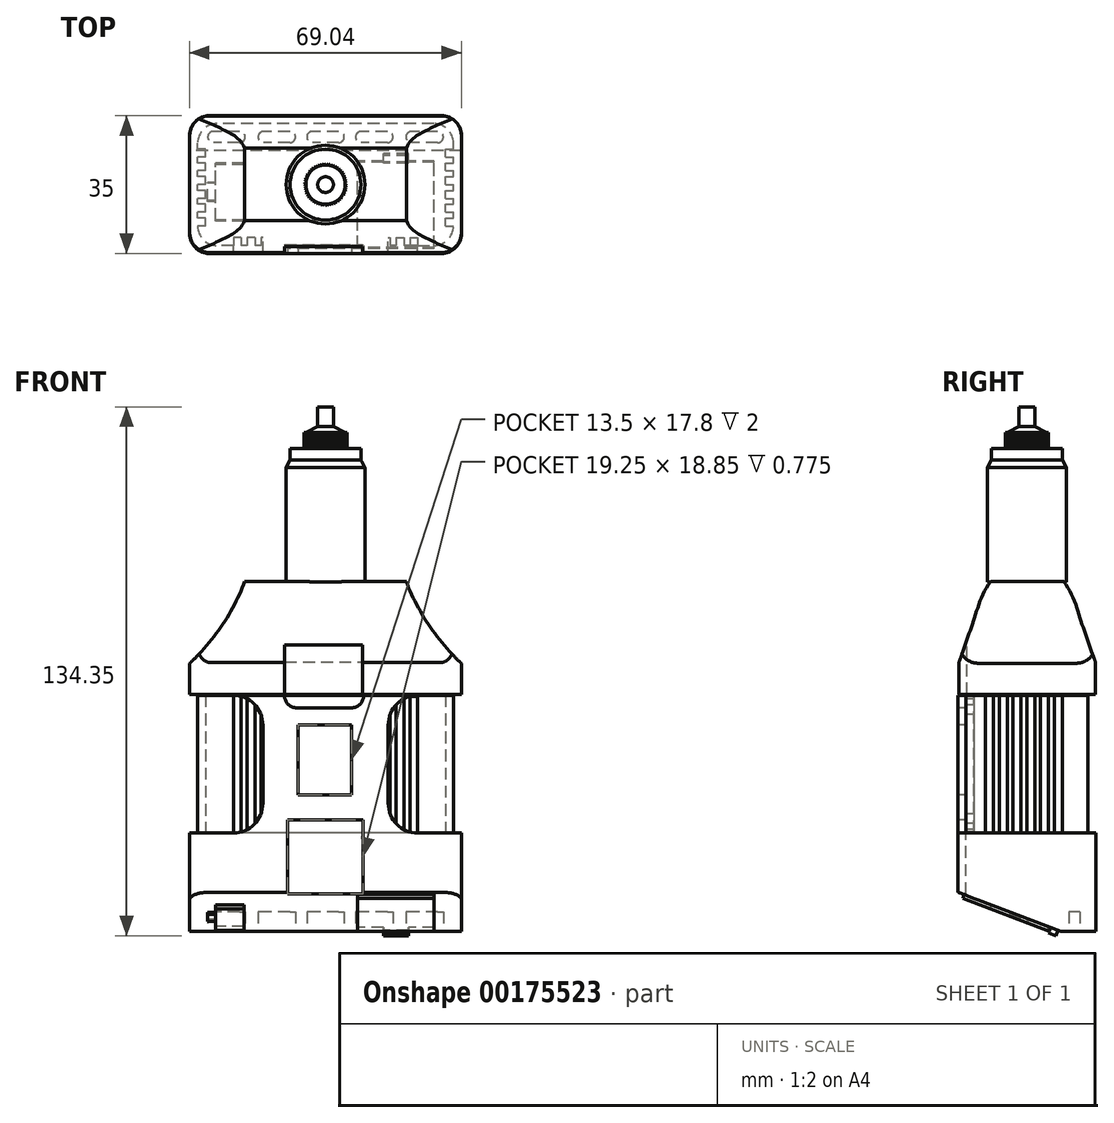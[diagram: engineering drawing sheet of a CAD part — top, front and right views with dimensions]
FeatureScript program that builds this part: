
annotation { "Feature Type Name" : "Feature", "Feature Type Description" : "" }
export const myFeature = defineFeature(function(context is Context, id is Id, definition is map)
    precondition{}
    {
        {
            var Q0;
            Q0=qCreatedBy(makeId("Front.planeOp"),FACE);
            var sketch = newSketch(context, id + "F0", { "sketchPlane" : qUnion([Q0])});
            skLineSegment(sketch, "E0.bottom", {"start": v(32.52, 25.25) * mm, "end": v(-32.53, 25.25) * mm});
            skLineSegment(sketch, "E0.top", {"start": v(32.53, -25.25) * mm, "end": v(-32.52, -25.25) * mm});
            skLineSegment(sketch, "E0.left", {"start": v(32.52, 25.25) * mm, "end": v(32.53, -25.25) * mm});
            skLineSegment(sketch, "E0.right", {"start": v(-32.53, 25.25) * mm, "end": v(-32.52, -25.25) * mm});
            skPoint(sketch, "E0.middle", {"position": v(0, 0) * mm});
            skSolve(sketch);
        }
        {
            var Q0;
            Q0=makeQuery(id+"F0.imprint","IMPRINT",FACE,{"disambiguationData":[TD([[makeQuery(id+"F0.imprint","IMPRINT",EDGE,{"derivedFrom":sQuery(id+"F0.wireOp",EDGE,"E0.bottom")}),1.0]])]});
            extrude(context, id + "F1", {"entities" : qUnion([Q0]), "endBound" : BoundingType.SYMMETRIC, "depth" : 31 * mm});
        }
        {
            var Q0;
            Q0=makeQuery(id+"F1.opExtrude","CAP_FACE",FACE,{"disambiguationData":[OSD([sQuery(id+"F0.wireOp",EDGE,"E0.bottom"),sQuery(id+"F0.wireOp",EDGE,"E0.top"),sQuery(id+"F0.wireOp",EDGE,"E0.left"),sQuery(id+"F0.wireOp",EDGE,"E0.right")])],"isStart":false});
            var sketch = newSketch(context, id + "F2", { "sketchPlane" : qUnion([Q0])});
            skLineSegment(sketch, "E1", {"start": v(-32.52, -9.75) * mm, "end": v(-23.43, -9.75) * mm});
            skLineSegment(sketch, "E2", {"start": v(-32.52, -25.25) * mm, "end": v(32.53, -25.25) * mm});
            skLineSegment(sketch, "E3", {"start": v(-15.93, 17.75) * mm, "end": v(-15.92, -2.25) * mm});
            skLineSegment(sketch, "E4", {"start": v(15.92, 17.75) * mm, "end": v(15.92, -2.25) * mm});
            skLineSegment(sketch, "E5", {"start": v(-32.52, -9.75) * mm, "end": v(-32.52, -25.25) * mm});
            skLineSegment(sketch, "E6", {"start": v(32.53, -9.75) * mm, "end": v(32.53, -25.25) * mm});
            skLineSegment(sketch, "E7.trimOffspring", {"start": v(23.43, -9.75) * mm, "end": v(32.53, -9.75) * mm});
            skArc(sketch, "E8", {"start": v(-23.43, -9.75) * mm, "mid": v(-18.12, -7.55) * mm, "end": v(-15.92, -2.25) * mm});
            skArc(sketch, "E9", {"start": v(15.92, -2.25) * mm, "mid": v(18.12, -7.55) * mm, "end": v(23.43, -9.75) * mm});
            skPoint(sketch, "E10.orphan", {"position": v(-15.93, 25.25) * mm});
            skPoint(sketch, "E11.start.orphan", {"position": v(-23.43, 25.25) * mm});
            skArc(sketch, "E12", {"start": v(-15.93, 17.75) * mm, "mid": v(-18.12, 23.05) * mm, "end": v(-23.43, 25.25) * mm});
            skPoint(sketch, "E13.orphan", {"position": v(15.92, 25.25) * mm});
            skPoint(sketch, "E14.trimOffspring.end.orphan", {"position": v(32.52, 17.75) * mm});
            skLineSegment(sketch, "E15.trimOffspring", {"start": v(15.92, 25.25) * mm, "end": v(-15.93, 25.25) * mm});
            skPoint(sketch, "E16.trimOffspring.end.orphan", {"position": v(32.53, -2.25) * mm});
            skArc(sketch, "E17", {"start": v(23.42, 25.25) * mm, "mid": v(18.12, 23.05) * mm, "end": v(15.92, 17.75) * mm});
            skLineSegment(sketch, "E18", {"start": v(-23.43, 25.25) * mm, "end": v(-15.93, 25.25) * mm});
            skLineSegment(sketch, "E19", {"start": v(15.92, 25.25) * mm, "end": v(23.42, 25.25) * mm});
            skPoint(sketch, "E20.start.orphan", {"position": v(32.52, 25.25) * mm});
            skSolve(sketch);
        }
        {
            var Q0;
            Q0=qSketchRegion(id+"F2",true);
            extrude(context, id + "F3", {"entities" : qUnion([Q0]), "operationType" : NewBodyOperationType.ADD, "depth" : 2 * mm});
        }
        {
            var Q0;
            Q0=makeQuery(id+"F3.opExtrude","CAP_FACE",FACE,{"disambiguationData":[OSD([sQuery(id+"F2.wireOp",EDGE,"E1"),sQuery(id+"F2.wireOp",EDGE,"E2"),sQuery(id+"F2.wireOp",EDGE,"E3"),sQuery(id+"F2.wireOp",EDGE,"E4"),sQuery(id+"F2.wireOp",EDGE,"E5"),sQuery(id+"F2.wireOp",EDGE,"E6"),sQuery(id+"F2.wireOp",EDGE,"E7.trimOffspring"),sQuery(id+"F2.wireOp",EDGE,"E8"),sQuery(id+"F2.wireOp",EDGE,"E9"),sQuery(id+"F2.wireOp",EDGE,"E12"),sQuery(id+"F2.wireOp",EDGE,"E15.trimOffspring"),sQuery(id+"F2.wireOp",EDGE,"E17"),sQuery(id+"F2.wireOp",EDGE,"E18"),sQuery(id+"F2.wireOp",EDGE,"E19")])],"isStart":false});
            var sketch = newSketch(context, id + "F4", { "sketchPlane" : qUnion([Q0])});
            skLineSegment(sketch, "E21", {"start": v(-15.93, 17.75) * mm, "end": v(15.92, 17.75) * mm, "construction": true});
            skLineSegment(sketch, "E22.bottom", {"start": v(-6.93, 17.75) * mm, "end": v(6.57, 17.75) * mm});
            skLineSegment(sketch, "E22.top", {"start": v(-6.93, -0.05) * mm, "end": v(6.57, -0.05) * mm});
            skLineSegment(sketch, "E22.left", {"start": v(-6.93, 17.75) * mm, "end": v(-6.93, -0.05) * mm});
            skLineSegment(sketch, "E22.right", {"start": v(6.57, 17.75) * mm, "end": v(6.57, -0.05) * mm});
            skLineSegment(sketch, "E23", {"start": v(-7.26, 22.05) * mm, "end": v(6.5, 22.05) * mm});
            skPoint(sketch, "E24.start.orphan", {"position": v(9.39, 25.25) * mm});
            skArc(sketch, "E25", {"start": v(6.5, 22.05) * mm, "mid": v(8.76, 22.99) * mm, "end": v(9.7, 25.25) * mm});
            skPoint(sketch, "E26.orphan", {"position": v(-10.85, 25.25) * mm});
            skArc(sketch, "E27", {"start": v(-7.26, 22.05) * mm, "mid": v(-9.52, 22.99) * mm, "end": v(-10.46, 25.25) * mm});
            skLineSegment(sketch, "E28", {"start": v(-9.7, -25.25) * mm, "end": v(-9.7, -6.4) * mm});
            skLineSegment(sketch, "E29", {"start": v(-9.7, -6.4) * mm, "end": v(9.56, -6.4) * mm});
            skLineSegment(sketch, "E30", {"start": v(9.56, -6.4) * mm, "end": v(9.56, -25.25) * mm});
            skSolve(sketch);
        }
        {
            var Q0;
            Q0=makeQuery(id+"F3.boolean.opBoolean","MERGE",FACE,{"derivedFrom":[makeQuery(id+"F1.opExtrude","SWEPT_FACE",FACE,{"disambiguationData":[OSD([sQuery(id+"F0.wireOp",EDGE,"E0.top")])]}),makeQuery(id+"F3.opExtrude","SWEPT_FACE",FACE,{"disambiguationData":[OSD([sQuery(id+"F2.wireOp",EDGE,"E2")])]})]});
            var sketch = newSketch(context, id + "F5", { "sketchPlane" : qUnion([Q0])});
            skLineSegment(sketch, "E31.bottom", {"start": v(-32.52, 17.5) * mm, "end": v(32.53, 17.5) * mm});
            skLineSegment(sketch, "E31.top", {"start": v(-32.52, -15.5) * mm, "end": v(32.53, -15.5) * mm});
            skLineSegment(sketch, "E31.left", {"start": v(-32.52, 17.5) * mm, "end": v(-32.52, -15.5) * mm});
            skLineSegment(sketch, "E31.right", {"start": v(32.53, 17.5) * mm, "end": v(32.53, -15.5) * mm});
            skSolve(sketch);
        }
        {
            var Q0;
            Q0=qSketchRegion(id+"F5",true);
            extrude(context, id + "F6", {"entities" : qUnion([Q0]), "operationType" : NewBodyOperationType.ADD, "depth" : 9.5 * mm});
        }
        {
            var Q0;
            Q0=makeQuery(id+"F6.boolean.opBoolean","MERGE",FACE,{"derivedFrom":[makeQuery(id+"F3.boolean.opBoolean","MERGE",FACE,{"derivedFrom":[makeQuery(id+"F1.opExtrude","SWEPT_FACE",FACE,{"disambiguationData":[OSD([sQuery(id+"F0.wireOp",EDGE,"E0.right")])]}),makeQuery(id+"F3.opExtrude","SWEPT_FACE",FACE,{"disambiguationData":[OSD([sQuery(id+"F2.wireOp",EDGE,"E5")])]})]}),makeQuery(id+"F6.opExtrude","SWEPT_FACE",FACE,{"disambiguationData":[OSD([sQuery(id+"F5.wireOp",EDGE,"E31.left")])]})]});
            var sketch = newSketch(context, id + "F7", { "sketchPlane" : qUnion([Q0])});
            skLineSegment(sketch, "E32", {"start": v(-8.68, -34.75) * mm, "end": v(17.5, -24.78) * mm});
            skLineSegment(sketch, "E33", {"start": v(17.5, -24.78) * mm, "end": v(17.5, -34.75) * mm});
            skLineSegment(sketch, "E34", {"start": v(17.5, -34.75) * mm, "end": v(-8.68, -34.75) * mm});
            skSolve(sketch);
        }
        {
            var Q0;
            Q0=qSketchRegion(id+"F7",true);
            extrude(context, id + "F8", {"entities" : qUnion([Q0]), "operationType" : NewBodyOperationType.REMOVE, "endBound" : BoundingType.THROUGH_ALL, "oppositeDirection" : true, "depth" : 25 * mm});
        }
        {
            var Q0;
            Q0=qSketchRegion(id+"F4",true);
            extrude(context, id + "F9", {"entities" : qUnion([Q0]), "operationType" : NewBodyOperationType.REMOVE, "oppositeDirection" : true, "depth" : 2 * mm});
        }
        {
            var Q0;
            {var subQ0=sQuery(id+"F4.wireOp",EDGE,"E28");Q0=makeQuery(id+"F4.imprint","IMPRINT",FACE,{"disambiguationData":[TD([[makeQuery(id+"F4.imprint","IMPRINT",EDGE,{"derivedFrom":subQ0}),-1.0]])]});}
            extrude(context, id + "F10", {"entities" : qUnion([Q0]), "operationType" : NewBodyOperationType.REMOVE, "oppositeDirection" : true, "depth" : 2 * mm});
        }
        {
            var Q0;
            Q0=makeQuery(id+"F4.imprint","IMPRINT",FACE,{"disambiguationData":[TD([[makeQuery(id+"F4.imprint","IMPRINT",EDGE,{"derivedFrom":sQuery(id+"F4.wireOp",EDGE,"E23")}),1.0]])]});
            extrude(context, id + "F11", {"entities" : qUnion([Q0]), "operationType" : NewBodyOperationType.REMOVE, "oppositeDirection" : true, "depth" : 2 * mm});
        }
        {
            var Q0;
            Q0=makeQuery(id+"F6.opExtrude","CAP_FACE",FACE,{"disambiguationData":[OSD([sQuery(id+"F5.wireOp",EDGE,"E31.bottom"),sQuery(id+"F5.wireOp",EDGE,"E31.top"),sQuery(id+"F5.wireOp",EDGE,"E31.left"),sQuery(id+"F5.wireOp",EDGE,"E31.right")])],"isStart":false});
            var sketch = newSketch(context, id + "F12", { "sketchPlane" : qUnion([Q0])});
            skLineSegment(sketch, "E35.bottom", {"start": v(-21.85, -10.66) * mm, "end": v(-28.5, -10.66) * mm});
            skLineSegment(sketch, "E35.top", {"start": v(-21.85, -13.51) * mm, "end": v(-28.5, -13.51) * mm});
            skPoint(sketch, "E35.middle", {"position": v(-25.17, -12.1) * mm});
            skLineSegment(sketch, "E36.bottom", {"start": v(-9.07, -10.66) * mm, "end": v(-15.71, -10.66) * mm});
            skLineSegment(sketch, "E36.top", {"start": v(-9.07, -13.52) * mm, "end": v(-15.71, -13.52) * mm});
            skPoint(sketch, "E36.middle", {"position": v(-12.39, -12.09) * mm});
            skLineSegment(sketch, "E37.bottom", {"start": v(3.32, -10.66) * mm, "end": v(-3.32, -10.66) * mm});
            skLineSegment(sketch, "E37.top", {"start": v(3.33, -13.52) * mm, "end": v(-3.32, -13.52) * mm});
            skPoint(sketch, "E37.middle", {"position": v(0, -12.1) * mm});
            skLineSegment(sketch, "E38.bottom", {"start": v(15.71, -10.67) * mm, "end": v(9.06, -10.67) * mm});
            skLineSegment(sketch, "E38.top", {"start": v(15.71, -13.51) * mm, "end": v(9.06, -13.51) * mm});
            skPoint(sketch, "E38.middle", {"position": v(12.39, -12.09) * mm});
            skLineSegment(sketch, "E39.bottom", {"start": v(28.5, -10.66) * mm, "end": v(21.85, -10.66) * mm});
            skLineSegment(sketch, "E39.top", {"start": v(28.5, -13.51) * mm, "end": v(21.85, -13.51) * mm});
            skPoint(sketch, "E39.middle", {"position": v(25.18, -12.09) * mm});
            skArc(sketch, "E40", {"start": v(-28.5, -10.66) * mm, "mid": v(-29.92, -12.09) * mm, "end": v(-28.5, -13.51) * mm});
            skArc(sketch, "E41", {"start": v(-21.85, -10.67) * mm, "mid": v(-20.42, -12.1) * mm, "end": v(-21.85, -13.51) * mm});
            skArc(sketch, "E42", {"start": v(28.5, -10.66) * mm, "mid": v(29.93, -12.09) * mm, "end": v(28.5, -13.51) * mm});
            skArc(sketch, "E43", {"start": v(21.85, -10.66) * mm, "mid": v(20.43, -12.09) * mm, "end": v(21.85, -13.51) * mm});
            skArc(sketch, "E44", {"start": v(-3.33, -13.52) * mm, "mid": v(-4.75, -12.1) * mm, "end": v(-3.32, -10.66) * mm});
            skArc(sketch, "E45", {"start": v(3.32, -10.67) * mm, "mid": v(4.75, -12.1) * mm, "end": v(3.33, -13.52) * mm});
            skArc(sketch, "E46", {"start": v(-9.07, -10.66) * mm, "mid": v(-7.64, -12.09) * mm, "end": v(-9.07, -13.52) * mm});
            skArc(sketch, "E47", {"start": v(-15.71, -10.66) * mm, "mid": v(-17.14, -12.09) * mm, "end": v(-15.71, -13.52) * mm});
            skArc(sketch, "E48", {"start": v(15.71, -10.67) * mm, "mid": v(17.14, -12.1) * mm, "end": v(15.71, -13.51) * mm});
            skArc(sketch, "E49", {"start": v(9.06, -10.67) * mm, "mid": v(7.64, -12.1) * mm, "end": v(9.06, -13.51) * mm});
            skSolve(sketch);
        }
        {
            var Q0;
            Q0=qSketchRegion(id+"F12",true);
            extrude(context, id + "F13", {"entities" : qUnion([Q0]), "operationType" : NewBodyOperationType.REMOVE, "oppositeDirection" : true, "depth" : 5 * mm});
        }
        {
            var Q0;
            Q0=makeQuery(id+"F6.boolean.opBoolean","MERGE",FACE,{"derivedFrom":[makeQuery(id+"F3.boolean.opBoolean","MERGE",FACE,{"derivedFrom":[makeQuery(id+"F1.opExtrude","SWEPT_FACE",FACE,{"disambiguationData":[OSD([sQuery(id+"F0.wireOp",EDGE,"E0.right")])]}),makeQuery(id+"F3.opExtrude","SWEPT_FACE",FACE,{"disambiguationData":[OSD([sQuery(id+"F2.wireOp",EDGE,"E5")])]})]}),makeQuery(id+"F6.opExtrude","SWEPT_FACE",FACE,{"disambiguationData":[OSD([sQuery(id+"F5.wireOp",EDGE,"E31.left")])]})]});
            var sketch = newSketch(context, id + "F14", { "sketchPlane" : qUnion([Q0])});
            skLineSegment(sketch, "E50", {"start": v(17.5, -9.75) * mm, "end": v(-15.5, -9.75) * mm});
            skLineSegment(sketch, "E51", {"start": v(-15.5, -9.75) * mm, "end": v(-15.5, -34.75) * mm});
            skLineSegment(sketch, "E52", {"start": v(-15.5, -34.75) * mm, "end": v(-8.68, -34.75) * mm});
            skLineSegment(sketch, "E53", {"start": v(-8.68, -34.75) * mm, "end": v(17.5, -24.78) * mm});
            skLineSegment(sketch, "E54", {"start": v(17.5, -24.78) * mm, "end": v(17.5, -9.75) * mm});
            skSolve(sketch);
        }
        {
            var Q0;
            Q0=qSketchRegion(id+"F14",true);
            extrude(context, id + "F15", {"entities" : qUnion([Q0]), "operationType" : NewBodyOperationType.ADD, "depth" : 2 * mm});
        }
        {
            var Q0;
            Q0=makeQuery(id+"F6.boolean.opBoolean","MERGE",FACE,{"derivedFrom":[makeQuery(id+"F3.boolean.opBoolean","MERGE",FACE,{"derivedFrom":[makeQuery(id+"F1.opExtrude","SWEPT_FACE",FACE,{"disambiguationData":[OSD([sQuery(id+"F0.wireOp",EDGE,"E0.left")])]}),makeQuery(id+"F3.opExtrude","SWEPT_FACE",FACE,{"disambiguationData":[OSD([sQuery(id+"F2.wireOp",EDGE,"E6")])]})]}),makeQuery(id+"F6.opExtrude","SWEPT_FACE",FACE,{"disambiguationData":[OSD([sQuery(id+"F5.wireOp",EDGE,"E31.right")])]})]});
            var sketch = newSketch(context, id + "F16", { "sketchPlane" : qUnion([Q0])});
            skLineSegment(sketch, "E55", {"start": v(-17.5, -9.75) * mm, "end": v(15.5, -9.75) * mm});
            skLineSegment(sketch, "E56", {"start": v(15.5, -9.75) * mm, "end": v(15.5, -34.75) * mm});
            skLineSegment(sketch, "E57", {"start": v(15.5, -34.75) * mm, "end": v(8.68, -34.75) * mm});
            skLineSegment(sketch, "E58", {"start": v(8.68, -34.75) * mm, "end": v(-17.5, -24.78) * mm});
            skLineSegment(sketch, "E59", {"start": v(-17.5, -24.78) * mm, "end": v(-17.5, -9.75) * mm});
            skSolve(sketch);
        }
        {
            var Q0;
            Q0=qSketchRegion(id+"F16",true);
            extrude(context, id + "F17", {"entities" : qUnion([Q0]), "operationType" : NewBodyOperationType.ADD, "depth" : 2 * mm});
        }
        {
            var Q0;
            Q0=makeQuery(id+"F17.boolean.opBoolean","MERGE",FACE,{"derivedFrom":[makeQuery(id+"F15.boolean.opBoolean","MERGE",FACE,{"derivedFrom":[makeQuery(id+"F6.boolean.opBoolean","MERGE",FACE,{"derivedFrom":[makeQuery(id+"F1.opExtrude","CAP_FACE",FACE,{"disambiguationData":[OSD([sQuery(id+"F0.wireOp",EDGE,"E0.bottom"),sQuery(id+"F0.wireOp",EDGE,"E0.top"),sQuery(id+"F0.wireOp",EDGE,"E0.left"),sQuery(id+"F0.wireOp",EDGE,"E0.right")])],"isStart":true}),makeQuery(id+"F6.opExtrude","SWEPT_FACE",FACE,{"disambiguationData":[OSD([sQuery(id+"F5.wireOp",EDGE,"E31.top")])]})]}),makeQuery(id+"F15.opExtrude","SWEPT_FACE",FACE,{"disambiguationData":[OSD([sQuery(id+"F14.wireOp",EDGE,"E51")])]})]}),makeQuery(id+"F17.opExtrude","SWEPT_FACE",FACE,{"disambiguationData":[OSD([sQuery(id+"F16.wireOp",EDGE,"E56")])]})]});
            var sketch = newSketch(context, id + "F18", { "sketchPlane" : qUnion([Q0])});
            skLineSegment(sketch, "E60", {"start": v(-34.53, -9.75) * mm, "end": v(34.52, -9.75) * mm});
            skLineSegment(sketch, "E61", {"start": v(-34.53, -9.75) * mm, "end": v(-34.53, -34.75) * mm});
            skLineSegment(sketch, "E62", {"start": v(-34.53, -34.75) * mm, "end": v(34.52, -34.75) * mm});
            skLineSegment(sketch, "E63", {"start": v(34.52, -34.75) * mm, "end": v(34.52, -9.75) * mm});
            skSolve(sketch);
        }
        {
            var Q0;
            Q0=qSketchRegion(id+"F18",true);
            extrude(context, id + "F19", {"entities" : qUnion([Q0]), "operationType" : NewBodyOperationType.ADD, "depth" : 2 * mm});
        }
        {
            var Q0;
            Q0=makeQuery(id+"F17.boolean.opBoolean","MERGE",FACE,{"derivedFrom":[makeQuery(id+"F15.boolean.opBoolean","MERGE",FACE,{"derivedFrom":[makeQuery(id+"F8.boolean.opBoolean","COPY",FACE,{"derivedFrom":makeQuery(id+"F8.opExtrude","SWEPT_FACE",FACE,{"disambiguationData":[OSD([sQuery(id+"F7.wireOp",EDGE,"E32")])]})}),makeQuery(id+"F15.opExtrude","SWEPT_FACE",FACE,{"disambiguationData":[OSD([sQuery(id+"F14.wireOp",EDGE,"E53")])]})]}),makeQuery(id+"F17.opExtrude","SWEPT_FACE",FACE,{"disambiguationData":[OSD([sQuery(id+"F16.wireOp",EDGE,"E58")])]})]});
            var sketch = newSketch(context, id + "F20", { "sketchPlane" : qUnion([Q0])});
            skLineSegment(sketch, "E64.bottom", {"start": v(27.6, 5.87) * mm, "end": v(8.1, 5.87) * mm});
            skLineSegment(sketch, "E64.top", {"start": v(27.6, -17.63) * mm, "end": v(8.1, -17.63) * mm});
            skLineSegment(sketch, "E64.left", {"start": v(27.6, 5.87) * mm, "end": v(27.6, -17.63) * mm});
            skLineSegment(sketch, "E64.right", {"start": v(8.1, 5.87) * mm, "end": v(8.1, -17.63) * mm});
            skPoint(sketch, "E64.middle", {"position": v(17.85, -5.88) * mm});
            skLineSegment(sketch, "E65.bottom", {"start": v(-20.69, -1.6) * mm, "end": v(-27.99, -1.6) * mm});
            skLineSegment(sketch, "E65.top", {"start": v(-20.69, -17) * mm, "end": v(-27.99, -17) * mm});
            skLineSegment(sketch, "E65.left", {"start": v(-20.69, -1.6) * mm, "end": v(-20.69, -17) * mm});
            skLineSegment(sketch, "E65.right", {"start": v(-27.99, -1.6) * mm, "end": v(-27.99, -17) * mm});
            skPoint(sketch, "E65.middle", {"position": v(-24.34, -9.3) * mm});
            skLineSegment(sketch, "E66.bottom", {"start": v(-27.99, -6.8) * mm, "end": v(-29.99, -6.8) * mm});
            skLineSegment(sketch, "E66.top", {"start": v(-27.99, -11.8) * mm, "end": v(-29.99, -11.8) * mm});
            skLineSegment(sketch, "E66.left", {"start": v(-27.99, -6.8) * mm, "end": v(-27.99, -11.8) * mm});
            skLineSegment(sketch, "E66.right", {"start": v(-29.99, -6.8) * mm, "end": v(-29.99, -11.8) * mm});
            skPoint(sketch, "E66.middle", {"position": v(-28.99, -9.3) * mm});
            skPoint(sketch, "E66.middle.positionSnap0", {"position": v(-27.99, -9.3) * mm});
            skPoint(sketch, "E66.centerSnap0", {"position": v(-27.99, -9.3) * mm});
            skLineSegment(sketch, "E67.bottom", {"start": v(21.03, -17.63) * mm, "end": v(14.68, -17.63) * mm});
            skLineSegment(sketch, "E67.top", {"start": v(21.03, -19.63) * mm, "end": v(14.68, -19.63) * mm});
            skLineSegment(sketch, "E67.left", {"start": v(21.03, -17.63) * mm, "end": v(21.03, -19.63) * mm});
            skLineSegment(sketch, "E67.right", {"start": v(14.68, -17.63) * mm, "end": v(14.68, -19.63) * mm});
            skPoint(sketch, "E67.middle", {"position": v(17.85, -18.63) * mm});
            skPoint(sketch, "E67.middle.positionSnap0", {"position": v(17.85, -17.63) * mm});
            skPoint(sketch, "E67.centerSnap0", {"position": v(17.85, -17.63) * mm});
            skSolve(sketch);
        }
        {
            var Q0;
            Q0=qCreatedBy(makeId("Right.planeOp"),FACE);
            cPlane(context, id + "F21", {"entities" : qUnion([Q0]), "cplaneType" : CPlaneType.OFFSET, "offset" : 34.5 * mm, "width" : 150 * mm, "height" : 150 * mm});
        }
        {
            var Q0;
            Q0=qCreatedBy(id+"F21.planeOp",FACE);
            var sketch = newSketch(context, id + "F22", { "sketchPlane" : qUnion([Q0])});
            skLineSegment(sketch, "E68.bottom", {"start": v(-17.27, 25.48) * mm, "end": v(17.46, 25.48) * mm});
            skLineSegment(sketch, "E68.top", {"start": v(-17.27, 58.58) * mm, "end": v(17.46, 58.58) * mm});
            skLineSegment(sketch, "E68.left", {"start": v(-17.27, 25.48) * mm, "end": v(-17.27, 58.58) * mm});
            skLineSegment(sketch, "E68.right", {"start": v(17.46, 25.48) * mm, "end": v(17.46, 58.58) * mm});
            skSolve(sketch);
        }
        {
            var Q0;
            Q0=qSketchRegion(id+"F22",true);
            extrude(context, id + "F23", {"entities" : qUnion([Q0]), "oppositeDirection" : true, "depth" : 69 * mm});
        }
        {
            var Q0;
            Q0=makeQuery(id+"F23.opExtrude","SWEPT_FACE",FACE,{"disambiguationData":[OSD([sQuery(id+"F22.wireOp",EDGE,"E68.left")])]});
            var sketch = newSketch(context, id + "F24", { "sketchPlane" : qUnion([Q0])});
            skLineSegment(sketch, "E69", {"start": v(-34.5, 25.48) * mm, "end": v(-34.5, 33.38) * mm});
            skLineSegment(sketch, "E70", {"start": v(34.5, 25.48) * mm, "end": v(34.5, 33.38) * mm});
            skArc(sketch, "E71", {"start": v(-34.5, 33.38) * mm, "mid": v(-25.06, 44.94) * mm, "end": v(-19, 58.58) * mm});
            skArc(sketch, "E72", {"start": v(19, 58.58) * mm, "mid": v(25.06, 44.94) * mm, "end": v(34.5, 33.38) * mm});
            skLineSegment(sketch, "E73", {"start": v(-19, 58.58) * mm, "end": v(-34.5, 58.58) * mm});
            skLineSegment(sketch, "E74", {"start": v(-34.5, 58.58) * mm, "end": v(-34.5, 33.38) * mm});
            skLineSegment(sketch, "E75", {"start": v(19, 58.58) * mm, "end": v(34.5, 58.58) * mm});
            skLineSegment(sketch, "E76", {"start": v(34.5, 58.58) * mm, "end": v(34.5, 33.38) * mm});
            skSolve(sketch);
        }
        {
            var Q0;
            Q0=qSketchRegion(id+"F24",true);
            extrude(context, id + "F25", {"entities" : qUnion([Q0]), "operationType" : NewBodyOperationType.REMOVE, "endBound" : BoundingType.THROUGH_ALL, "oppositeDirection" : true, "depth" : 25 * mm});
        }
        {
            var Q0;
            Q0=qCreatedBy(makeId("Right.planeOp"),FACE);
            cPlane(context, id + "F26", {"entities" : qUnion([Q0]), "cplaneType" : CPlaneType.OFFSET, "offset" : 34.5 * mm, "oppositeDirection" : true, "width" : 150 * mm, "height" : 150 * mm});
        }
        {
            var Q0;
            Q0=qCreatedBy(id+"F26.planeOp",FACE);
            var sketch = newSketch(context, id + "F27", { "sketchPlane" : qUnion([Q0])});
            skPoint(sketch, "E77", {"position": v(0, 58.6) * mm});
            skPoint(sketch, "E78", {"position": v(-17.3, 33.51) * mm});
            skPoint(sketch, "E79", {"position": v(17.49, 33.51) * mm});
            skPoint(sketch, "E80", {"position": v(-9.07, 54.2) * mm});
            skPoint(sketch, "E81", {"position": v(-13.46, 44.5) * mm});
            skPoint(sketch, "E82", {"position": v(13.64, 44.5) * mm});
            skPoint(sketch, "E83", {"position": v(9.26, 54.2) * mm});
            skFitSpline(sketch, "E84", {"points": [v(17.49, 33.51) * mm, v(13.64, 44.5) * mm, v(9.26, 54.2) * mm, v(0, 58.6) * mm, v(-9.07, 54.2) * mm, v(-13.46, 44.5) * mm, v(-17.3, 33.51) * mm], "startDerivative": vector(-23.18, 63.45) * mm, "endDerivative": vector(-23.08, -63.46) * mm});
            skLineSegment(sketch, "E85", {"start": v(17.49, 33.51) * mm, "end": v(17.49, 58.79) * mm});
            skLineSegment(sketch, "E86", {"start": v(17.49, 58.79) * mm, "end": v(-17.49, 58.6) * mm});
            skLineSegment(sketch, "E87", {"start": v(-17.49, 58.6) * mm, "end": v(-17.3, 33.51) * mm});
            skSolve(sketch);
        }
        {
            var Q0;
            Q0=qSketchRegion(id+"F27",true);
            extrude(context, id + "F28", {"entities" : qUnion([Q0]), "operationType" : NewBodyOperationType.REMOVE, "endBound" : BoundingType.THROUGH_ALL, "depth" : 25 * mm});
        }
        {
            var Q0;
            Q0=makeQuery(id+"F23.opExtrude","SWEPT_FACE",FACE,{"disambiguationData":[OSD([sQuery(id+"F22.wireOp",EDGE,"E68.left")])]});
            var sketch = newSketch(context, id + "F29", { "sketchPlane" : qUnion([Q0])});
            skLineSegment(sketch, "E88.bottom", {"start": v(-10.4, 25.48) * mm, "end": v(9.39, 25.48) * mm});
            skLineSegment(sketch, "E88.top", {"start": v(-10.4, 37.98) * mm, "end": v(9.39, 37.98) * mm});
            skLineSegment(sketch, "E88.left", {"start": v(-10.4, 25.48) * mm, "end": v(-10.4, 37.98) * mm});
            skLineSegment(sketch, "E88.right", {"start": v(9.39, 25.48) * mm, "end": v(9.39, 37.98) * mm});
            skSolve(sketch);
        }
        {
            var Q0;
            Q0=qSketchRegion(id+"F29",true);
            extrude(context, id + "F30", {"entities" : qUnion([Q0]), "operationType" : NewBodyOperationType.REMOVE, "oppositeDirection" : true, "depth" : 2 * mm});
        }
        {
            var Q0;
            Q0=qSketchRegion(id+"F20",true);
            extrude(context, id + "F31", {"entities" : qUnion([Q0]), "operationType" : NewBodyOperationType.ADD, "depth" : 1 * mm});
        }
        {
            var Q0;
            Q0=makeQuery(id+"F31.opExtrude","CAP_FACE",FACE,{"disambiguationData":[OSD([sQuery(id+"F20.wireOp",EDGE,"E65.bottom"),sQuery(id+"F20.wireOp",EDGE,"E65.top"),sQuery(id+"F20.wireOp",EDGE,"E65.left"),sQuery(id+"F20.wireOp",EDGE,"E65.right"),sQuery(id+"F20.wireOp",EDGE,"E66.bottom"),sQuery(id+"F20.wireOp",EDGE,"E66.top"),sQuery(id+"F20.wireOp",EDGE,"E66.right")])],"isStart":false});
            var sketch = newSketch(context, id + "F32", { "sketchPlane" : qUnion([Q0])});
            skLineSegment(sketch, "E89", {"start": v(-27.99, -6.8) * mm, "end": v(-27.99, -11.8) * mm});
            skLineSegment(sketch, "E90", {"start": v(-27.99, -11.8) * mm, "end": v(-29.99, -11.8) * mm});
            skLineSegment(sketch, "E91", {"start": v(-29.99, -11.8) * mm, "end": v(-29.99, -6.8) * mm});
            skLineSegment(sketch, "E92", {"start": v(-29.99, -6.8) * mm, "end": v(-27.99, -6.8) * mm});
            skSolve(sketch);
        }
        {
            var Q0;
            Q0=qSketchRegion(id+"F32",true);
            extrude(context, id + "F33", {"entities" : qUnion([Q0]), "operationType" : NewBodyOperationType.REMOVE, "oppositeDirection" : true, "depth" : 0.5 * mm});
        }
        {
            var Q0;
            Q0=makeQuery(id+"F31.opExtrude","CAP_FACE",FACE,{"disambiguationData":[OSD([sQuery(id+"F20.wireOp",EDGE,"E64.bottom"),sQuery(id+"F20.wireOp",EDGE,"E64.top"),sQuery(id+"F20.wireOp",EDGE,"E64.left"),sQuery(id+"F20.wireOp",EDGE,"E64.right"),sQuery(id+"F20.wireOp",EDGE,"E67.top"),sQuery(id+"F20.wireOp",EDGE,"E67.left"),sQuery(id+"F20.wireOp",EDGE,"E67.right")])],"isStart":false});
            var sketch = newSketch(context, id + "F34", { "sketchPlane" : qUnion([Q0])});
            skLineSegment(sketch, "E93", {"start": v(14.68, -17.63) * mm, "end": v(14.68, -19.63) * mm});
            skLineSegment(sketch, "E94", {"start": v(14.68, -19.63) * mm, "end": v(21.03, -19.63) * mm});
            skLineSegment(sketch, "E95", {"start": v(21.03, -19.63) * mm, "end": v(21.03, -17.63) * mm});
            skLineSegment(sketch, "E96", {"start": v(21.03, -17.63) * mm, "end": v(14.68, -17.63) * mm});
            skSolve(sketch);
        }
        {
            var Q0;
            Q0=qSketchRegion(id+"F34",true);
            extrude(context, id + "F35", {"entities" : qUnion([Q0]), "operationType" : NewBodyOperationType.ADD, "depth" : 0.5 * mm});
        }
        {
            var Q0;
            Q0=qCreatedBy(id+"F21.planeOp",FACE);
            cPlane(context, id + "F36", {"entities" : qUnion([Q0]), "cplaneType" : CPlaneType.OFFSET, "offset" : 34.5 * mm, "oppositeDirection" : true, "width" : 150 * mm, "height" : 150 * mm});
        }
        {
            var Q0;
            Q0=qCreatedBy(id+"F36.planeOp",FACE);
            var sketch = newSketch(context, id + "F37", { "sketchPlane" : qUnion([Q0])});
            skLineSegment(sketch, "E97", {"start": v(0, 56.65) * mm, "end": v(-12.82, 56.65) * mm});
            skLineSegment(sketch, "E98", {"start": v(-12.82, 56.65) * mm, "end": v(0, 56.65) * mm});
            skLineSegment(sketch, "E99", {"start": v(0, 56.65) * mm, "end": v(11.33, 56.65) * mm});
            skArc(sketch, "E100", {"start": v(5.67, 56.65) * mm, "mid": v(-0.37, 58.75) * mm, "end": v(-6.41, 56.65) * mm});
            skSolve(sketch);
        }
        {
            var Q0;
            Q0=qSketchRegion(id+"F37",true);
            extrude(context, id + "F38", {"entities" : qUnion([Q0]), "operationType" : NewBodyOperationType.REMOVE, "endBound" : BoundingType.THROUGH_ALL, "oppositeDirection" : true, "depth" : 25 * mm});
        }
        {
            var Q0;
            Q0=qSketchRegion(id+"F37",true);
            extrude(context, id + "F39", {"entities" : qUnion([Q0]), "operationType" : NewBodyOperationType.REMOVE, "endBound" : BoundingType.THROUGH_ALL, "depth" : 25 * mm});
        }
        {
            var Q0;
            Q0=qCreatedBy(id+"F36.planeOp",FACE);
            var sketch = newSketch(context, id + "F40", { "sketchPlane" : qUnion([Q0])});
            skLineSegment(sketch, "E101", {"start": v(5.61, 56.67) * mm, "end": v(0, 58.7) * mm});
            skLineSegment(sketch, "E102", {"start": v(0, 58.7) * mm, "end": v(5.06, 62.93) * mm});
            skLineSegment(sketch, "E103", {"start": v(5.06, 62.93) * mm, "end": v(10.3, 56.67) * mm});
            skLineSegment(sketch, "E104", {"start": v(10.3, 56.67) * mm, "end": v(5.61, 56.67) * mm});
            skSolve(sketch);
        }
        {
            var Q0;
            Q0=qSketchRegion(id+"F40",true);
            extrude(context, id + "F41", {"entities" : qUnion([Q0]), "operationType" : NewBodyOperationType.REMOVE, "endBound" : BoundingType.THROUGH_ALL, "oppositeDirection" : true, "depth" : 25 * mm});
        }
        {
            var Q0;
            Q0=qSketchRegion(id+"F40",true);
            extrude(context, id + "F42", {"entities" : qUnion([Q0]), "operationType" : NewBodyOperationType.REMOVE, "endBound" : BoundingType.THROUGH_ALL, "depth" : 25 * mm});
        }
        {
            var Q0;
            Q0=qCreatedBy(id+"F26.planeOp",FACE);
            var sketch = newSketch(context, id + "F43", { "sketchPlane" : qUnion([Q0])});
            skLineSegment(sketch, "E105", {"start": v(9.5, 54.11) * mm, "end": v(-9.29, 54.11) * mm});
            skLineSegment(sketch, "E106", {"start": v(-6.2, 56.8) * mm, "end": v(5.99, 56.8) * mm});
            skLineSegment(sketch, "E107", {"start": v(5.99, 56.8) * mm, "end": v(25.18, 56.8) * mm});
            skLineSegment(sketch, "E108", {"start": v(25.18, 56.8) * mm, "end": v(9.5, 54.11) * mm});
            skLineSegment(sketch, "E109", {"start": v(-9.29, 54.11) * mm, "end": v(-23.94, 54.11) * mm});
            skLineSegment(sketch, "E110", {"start": v(-23.94, 54.11) * mm, "end": v(-6.2, 56.8) * mm});
            skSolve(sketch);
        }
        {
            var Q0;
            Q0=qSketchRegion(id+"F43",true);
            extrude(context, id + "F44", {"entities" : qUnion([Q0]), "operationType" : NewBodyOperationType.REMOVE, "endBound" : BoundingType.THROUGH_ALL, "depth" : 25 * mm});
        }
        {
            var Q0;
            Q0=qCreatedBy(makeId("Front.planeOp"),FACE);
            var sketch = newSketch(context, id + "F45", { "sketchPlane" : qUnion([Q0])});
            skLineSegment(sketch, "E111", {"start": v(0, 88.2) * mm, "end": v(0, 41.26) * mm, "construction": true});
            skLineSegment(sketch, "E112", {"start": v(0, 54.1) * mm, "end": v(10, 54.1) * mm});
            skLineSegment(sketch, "E113", {"start": v(10, 54.1) * mm, "end": v(10, 83.1) * mm});
            skLineSegment(sketch, "E114", {"start": v(10, 83.1) * mm, "end": v(0, 83.1) * mm});
            skLineSegment(sketch, "E115", {"start": v(0, 83.1) * mm, "end": v(0, 54.1) * mm});
            skSolve(sketch);
        }
        {
            var Q0;
            Q0=makeQuery(id+"F45.imprint","IMPRINT",FACE,{"disambiguationData":[TD([[makeQuery(id+"F45.imprint","IMPRINT",EDGE,{"derivedFrom":sQuery(id+"F45.wireOp",EDGE,"E112")}),1.0]])]});
            var Q1;
            Q1=sQuery(id+"F45.wireOp",EDGE,"E111");
            revolve(context, id + "F46", {"operationType" : NewBodyOperationType.ADD, "entities" : qUnion([Q0]), "axis" : qUnion([Q1]), "revolveType" : RevolveType.FULL});
        }
        {
            var Q0;
            Q0=qCreatedBy(makeId("Top.planeOp"),FACE);
            cPlane(context, id + "F47", {"entities" : qUnion([Q0]), "cplaneType" : CPlaneType.OFFSET, "offset" : 85 * mm, "width" : 150 * mm, "height" : 150 * mm});
        }
        {
            var Q0;
            Q0=qCreatedBy(id+"F47.planeOp",FACE);
            var sketch = newSketch(context, id + "F48", { "sketchPlane" : qUnion([Q0])});
            skCircle(sketch, "E116", {"center": v(0, 0) * mm, "radius": 9 * mm});
            skSolve(sketch);
        }
        {
            var Q1;
            Q1=makeQuery(id+"F46.opRevolve","SWEPT_FACE",FACE,{"disambiguationData":[OSD([sQuery(id+"F45.wireOp",EDGE,"E114")])]});
            var Q2;
            Q2=makeQuery(id+"F48.imprint","IMPRINT",FACE,{"disambiguationData":[TD([[makeQuery(id+"F48.imprint","IMPRINT",EDGE,{"derivedFrom":sQuery(id+"F48.wireOp",EDGE,"E116")}),1.0]])]});
            loft(context, id + "F49", {"sheetProfilesArray" : [{ "sheetProfileEntities" : qUnion([Q1]) }, { "sheetProfileEntities" : qUnion([Q2]) }]});
        }
        {
            var Q0;
            Q0=makeQuery(id+"F49.opLoft","CAP_FACE",FACE,{"disambiguationData":[OSD([makeQuery(id+"F48.imprint","IMPRINT",FACE,{"disambiguationData":[TD([[makeQuery(id+"F48.imprint","IMPRINT",EDGE,{"derivedFrom":sQuery(id+"F48.wireOp",EDGE,"E116")}),1.0]])]})])],"isStart":true});
            var sketch = newSketch(context, id + "F50", { "sketchPlane" : qUnion([Q0])});
            skCircle(sketch, "E117", {"center": v(0, 0) * mm, "radius": 9 * mm});
            skSolve(sketch);
        }
        {
            var Q0;
            Q0=qSketchRegion(id+"F50",true);
            extrude(context, id + "F51", {"entities" : qUnion([Q0]), "operationType" : NewBodyOperationType.ADD, "depth" : 3 * mm});
        }
        {
            var Q0;
            Q0=makeQuery(id+"F51.opExtrude","CAP_FACE",FACE,{"disambiguationData":[OSD([sQuery(id+"F50.wireOp",EDGE,"E117")])],"isStart":false});
            var sketch = newSketch(context, id + "F52", { "sketchPlane" : qUnion([Q0])});
            skCircle(sketch, "E118", {"center": v(0, 0) * mm, "radius": 5 * mm});
            skCircle(sketch, "E119.cCircle", {"center": v(2.33, -4.42) * mm, "radius": 0.23 * mm, "construction": true});
            skLineSegment(sketch, "E119.0", {"start": v(2.56, -4.3) * mm, "end": v(2.56, -4.81) * mm});
            skLineSegment(sketch, "E119.1", {"start": v(2.56, -4.81) * mm, "end": v(2.1, -4.54) * mm});
            skPoint(sketch, "E119.0.midPoint", {"position": v(2.56, -4.42) * mm});
            skLineSegment(sketch, "E120.1.0", {"start": v(3.4, -3.67) * mm, "end": v(3.5, -4.18) * mm});
            skLineSegment(sketch, "E120.2.0", {"start": v(4.08, -2.88) * mm, "end": v(4.3, -3.36) * mm});
            skLineSegment(sketch, "E121.2.3.0", {"start": v(4.6, -1.97) * mm, "end": v(4.9, -2.39) * mm});
            skLineSegment(sketch, "E121.2.4.0", {"start": v(4.9, -0.97) * mm, "end": v(5.29, -1.32) * mm});
            skLineSegment(sketch, "E121.2.5.0", {"start": v(5, 0.07) * mm, "end": v(5.45, -0.2) * mm});
            skLineSegment(sketch, "E121.2.6.0", {"start": v(4.88, 1.1) * mm, "end": v(5.37, 0.95) * mm});
            skLineSegment(sketch, "E121.2.7.0", {"start": v(4.54, 2.1) * mm, "end": v(5.05, 2.04) * mm});
            skLineSegment(sketch, "E121.2.8.0", {"start": v(4, 3) * mm, "end": v(4.52, 3.05) * mm});
            skLineSegment(sketch, "E121.2.9.0", {"start": v(3.3, 3.76) * mm, "end": v(3.79, 3.92) * mm});
            skLineSegment(sketch, "E121.2.10.0", {"start": v(2.44, 4.36) * mm, "end": v(2.89, 4.62) * mm});
            skLineSegment(sketch, "E121.2.11.0", {"start": v(1.48, 4.78) * mm, "end": v(1.86, 5.12) * mm});
            skLineSegment(sketch, "E121.2.12.0", {"start": v(0.46, 4.98) * mm, "end": v(0.76, 5.4) * mm});
            skLineSegment(sketch, "E121.2.13.0", {"start": v(-0.6, 4.97) * mm, "end": v(-0.38, 5.44) * mm});
            skLineSegment(sketch, "E121.2.14.0", {"start": v(-1.6, 4.73) * mm, "end": v(-1.5, 5.24) * mm});
            skLineSegment(sketch, "E121.2.15.0", {"start": v(-2.56, 4.3) * mm, "end": v(-2.56, 4.81) * mm});
            skLineSegment(sketch, "E121.2.16.0", {"start": v(-3.4, 3.67) * mm, "end": v(-3.5, 4.18) * mm});
            skLineSegment(sketch, "E121.2.17.0", {"start": v(-4.08, 2.88) * mm, "end": v(-4.3, 3.36) * mm});
            skLineSegment(sketch, "E121.2.18.0", {"start": v(-4.6, 1.97) * mm, "end": v(-4.9, 2.39) * mm});
            skLineSegment(sketch, "E121.2.19.0", {"start": v(-4.9, 0.97) * mm, "end": v(-5.29, 1.32) * mm});
            skLineSegment(sketch, "E121.2.20.0", {"start": v(-5, -0.07) * mm, "end": v(-5.45, 0.2) * mm});
            skLineSegment(sketch, "E121.2.21.0", {"start": v(-4.88, -1.1) * mm, "end": v(-5.37, -0.95) * mm});
            skLineSegment(sketch, "E121.2.22.0", {"start": v(-4.54, -2.1) * mm, "end": v(-5.05, -2.04) * mm});
            skLineSegment(sketch, "E121.2.23.0", {"start": v(-4, -3) * mm, "end": v(-4.52, -3.05) * mm});
            skLineSegment(sketch, "E121.2.24.0", {"start": v(-3.3, -3.76) * mm, "end": v(-3.79, -3.92) * mm});
            skLineSegment(sketch, "E121.2.25.0", {"start": v(-2.44, -4.36) * mm, "end": v(-2.89, -4.62) * mm});
            skLineSegment(sketch, "E121.2.26.0", {"start": v(-1.48, -4.78) * mm, "end": v(-1.86, -5.12) * mm});
            skLineSegment(sketch, "E121.2.27.0", {"start": v(-0.46, -4.98) * mm, "end": v(-0.76, -5.4) * mm});
            skLineSegment(sketch, "E121.2.28.0", {"start": v(0.6, -4.97) * mm, "end": v(0.38, -5.44) * mm});
            skLineSegment(sketch, "E121.2.29.0", {"start": v(1.6, -4.73) * mm, "end": v(1.5, -5.24) * mm});
            skLineSegment(sketch, "E122.1.0", {"start": v(3.5, -4.18) * mm, "end": v(2.99, -4) * mm});
            skLineSegment(sketch, "E122.2.0", {"start": v(4.3, -3.36) * mm, "end": v(3.76, -3.3) * mm});
            skLineSegment(sketch, "E122.3.0", {"start": v(4.9, -2.39) * mm, "end": v(4.36, -2.45) * mm});
            skLineSegment(sketch, "E122.4.0", {"start": v(5.29, -1.32) * mm, "end": v(4.77, -1.49) * mm});
            skLineSegment(sketch, "E122.5.0", {"start": v(5.45, -0.2) * mm, "end": v(4.98, -0.46) * mm});
            skLineSegment(sketch, "E122.6.0", {"start": v(5.37, 0.95) * mm, "end": v(4.97, 0.58) * mm});
            skLineSegment(sketch, "E122.7.0", {"start": v(5.05, 2.04) * mm, "end": v(4.74, 1.6) * mm});
            skLineSegment(sketch, "E122.8.0", {"start": v(4.52, 3.05) * mm, "end": v(4.3, 2.55) * mm});
            skLineSegment(sketch, "E122.9.0", {"start": v(3.79, 3.92) * mm, "end": v(3.67, 3.4) * mm});
            skLineSegment(sketch, "E122.10.0", {"start": v(2.89, 4.62) * mm, "end": v(2.89, 4.08) * mm});
            skLineSegment(sketch, "E122.11.0", {"start": v(1.86, 5.12) * mm, "end": v(1.98, 4.6) * mm});
            skLineSegment(sketch, "E122.12.0", {"start": v(0.76, 5.4) * mm, "end": v(0.98, 4.9) * mm});
            skLineSegment(sketch, "E122.13.0", {"start": v(-0.38, 5.44) * mm, "end": v(-0.06, 5) * mm});
            skLineSegment(sketch, "E122.14.0", {"start": v(-1.5, 5.24) * mm, "end": v(-1.1, 4.88) * mm});
            skLineSegment(sketch, "E122.15.0", {"start": v(-2.56, 4.81) * mm, "end": v(-2.1, 4.54) * mm});
            skLineSegment(sketch, "E122.16.0", {"start": v(-3.5, 4.18) * mm, "end": v(-2.99, 4) * mm});
            skLineSegment(sketch, "E122.17.0", {"start": v(-4.3, 3.36) * mm, "end": v(-3.76, 3.3) * mm});
            skLineSegment(sketch, "E122.18.0", {"start": v(-4.9, 2.39) * mm, "end": v(-4.36, 2.45) * mm});
            skLineSegment(sketch, "E122.19.0", {"start": v(-5.29, 1.32) * mm, "end": v(-4.77, 1.49) * mm});
            skLineSegment(sketch, "E122.20.0", {"start": v(-5.45, 0.2) * mm, "end": v(-4.98, 0.46) * mm});
            skLineSegment(sketch, "E122.21.0", {"start": v(-5.37, -0.95) * mm, "end": v(-4.97, -0.58) * mm});
            skLineSegment(sketch, "E122.22.0", {"start": v(-5.05, -2.04) * mm, "end": v(-4.74, -1.6) * mm});
            skLineSegment(sketch, "E122.23.0", {"start": v(-4.52, -3.05) * mm, "end": v(-4.3, -2.55) * mm});
            skLineSegment(sketch, "E122.24.0", {"start": v(-3.79, -3.92) * mm, "end": v(-3.67, -3.4) * mm});
            skLineSegment(sketch, "E122.25.0", {"start": v(-2.89, -4.62) * mm, "end": v(-2.89, -4.08) * mm});
            skLineSegment(sketch, "E122.26.0", {"start": v(-1.86, -5.12) * mm, "end": v(-1.98, -4.6) * mm});
            skLineSegment(sketch, "E122.27.0", {"start": v(-0.76, -5.4) * mm, "end": v(-0.98, -4.9) * mm});
            skLineSegment(sketch, "E122.28.0", {"start": v(0.38, -5.44) * mm, "end": v(0.06, -5) * mm});
            skLineSegment(sketch, "E122.29.0", {"start": v(1.5, -5.24) * mm, "end": v(1.1, -4.88) * mm});
            skPoint(sketch, "E123.orphan", {"position": v(4.28, 2.12) * mm});
            skPoint(sketch, "E124.orphan", {"position": v(4.2, 2.33) * mm});
            skSolve(sketch);
        }
        {
            var Q0;
            Q0=qSketchRegion(id+"F52",true);
            extrude(context, id + "F53", {"entities" : qUnion([Q0]), "operationType" : NewBodyOperationType.ADD, "depth" : 4 * mm});
        }
        {
            var Q0;
            Q0=qCreatedBy(id+"F47.planeOp",FACE);
            cPlane(context, id + "F54", {"entities" : qUnion([Q0]), "cplaneType" : CPlaneType.OFFSET, "offset" : 8.5 * mm, "width" : 150 * mm, "height" : 150 * mm});
        }
        {
            var Q0;
            Q0=qCreatedBy(id+"F54.planeOp",FACE);
            var sketch = newSketch(context, id + "F55", { "sketchPlane" : qUnion([Q0])});
            skCircle(sketch, "E125", {"center": v(0, 0) * mm, "radius": 2 * mm});
            skSolve(sketch);
        }
        {
            var Q0;
            Q0=makeQuery(id+"F53.opExtrude","CAP_FACE",FACE,{"disambiguationData":[OSD([sQuery(id+"F52.wireOp",EDGE,"E118"),sQuery(id+"F52.wireOp",EDGE,"E119.0"),sQuery(id+"F52.wireOp",EDGE,"E119.1"),sQuery(id+"F52.wireOp",EDGE,"E120.1.0"),sQuery(id+"F52.wireOp",EDGE,"E120.2.0"),sQuery(id+"F52.wireOp",EDGE,"E121.2.3.0"),sQuery(id+"F52.wireOp",EDGE,"E121.2.4.0"),sQuery(id+"F52.wireOp",EDGE,"E121.2.5.0"),sQuery(id+"F52.wireOp",EDGE,"E121.2.6.0"),sQuery(id+"F52.wireOp",EDGE,"E121.2.7.0"),sQuery(id+"F52.wireOp",EDGE,"E121.2.8.0"),sQuery(id+"F52.wireOp",EDGE,"E121.2.9.0"),sQuery(id+"F52.wireOp",EDGE,"E121.2.10.0"),sQuery(id+"F52.wireOp",EDGE,"E121.2.11.0"),sQuery(id+"F52.wireOp",EDGE,"E121.2.12.0"),sQuery(id+"F52.wireOp",EDGE,"E121.2.13.0"),sQuery(id+"F52.wireOp",EDGE,"E121.2.14.0"),sQuery(id+"F52.wireOp",EDGE,"E121.2.15.0"),sQuery(id+"F52.wireOp",EDGE,"E121.2.16.0"),sQuery(id+"F52.wireOp",EDGE,"E121.2.17.0"),sQuery(id+"F52.wireOp",EDGE,"E121.2.18.0"),sQuery(id+"F52.wireOp",EDGE,"E121.2.19.0"),sQuery(id+"F52.wireOp",EDGE,"E121.2.20.0"),sQuery(id+"F52.wireOp",EDGE,"E121.2.21.0"),sQuery(id+"F52.wireOp",EDGE,"E121.2.22.0"),sQuery(id+"F52.wireOp",EDGE,"E121.2.23.0"),sQuery(id+"F52.wireOp",EDGE,"E121.2.24.0"),sQuery(id+"F52.wireOp",EDGE,"E121.2.25.0"),sQuery(id+"F52.wireOp",EDGE,"E121.2.26.0"),sQuery(id+"F52.wireOp",EDGE,"E121.2.27.0"),sQuery(id+"F52.wireOp",EDGE,"E121.2.28.0"),sQuery(id+"F52.wireOp",EDGE,"E121.2.29.0"),sQuery(id+"F52.wireOp",EDGE,"E122.1.0"),sQuery(id+"F52.wireOp",EDGE,"E122.2.0"),sQuery(id+"F52.wireOp",EDGE,"E122.3.0"),sQuery(id+"F52.wireOp",EDGE,"E122.4.0"),sQuery(id+"F52.wireOp",EDGE,"E122.5.0"),sQuery(id+"F52.wireOp",EDGE,"E122.6.0"),sQuery(id+"F52.wireOp",EDGE,"E122.7.0"),sQuery(id+"F52.wireOp",EDGE,"E122.8.0"),sQuery(id+"F52.wireOp",EDGE,"E122.9.0"),sQuery(id+"F52.wireOp",EDGE,"E122.10.0"),sQuery(id+"F52.wireOp",EDGE,"E122.11.0"),sQuery(id+"F52.wireOp",EDGE,"E122.12.0"),sQuery(id+"F52.wireOp",EDGE,"E122.13.0"),sQuery(id+"F52.wireOp",EDGE,"E122.14.0"),sQuery(id+"F52.wireOp",EDGE,"E122.15.0"),sQuery(id+"F52.wireOp",EDGE,"E122.16.0"),sQuery(id+"F52.wireOp",EDGE,"E122.17.0"),sQuery(id+"F52.wireOp",EDGE,"E122.18.0"),sQuery(id+"F52.wireOp",EDGE,"E122.19.0"),sQuery(id+"F52.wireOp",EDGE,"E122.20.0"),sQuery(id+"F52.wireOp",EDGE,"E122.21.0"),sQuery(id+"F52.wireOp",EDGE,"E122.22.0"),sQuery(id+"F52.wireOp",EDGE,"E122.23.0"),sQuery(id+"F52.wireOp",EDGE,"E122.24.0"),sQuery(id+"F52.wireOp",EDGE,"E122.25.0"),sQuery(id+"F52.wireOp",EDGE,"E122.26.0"),sQuery(id+"F52.wireOp",EDGE,"E122.27.0"),sQuery(id+"F52.wireOp",EDGE,"E122.28.0"),sQuery(id+"F52.wireOp",EDGE,"E122.29.0")])],"isStart":false});
            var sketch = newSketch(context, id + "F56", { "sketchPlane" : qUnion([Q0])});
            skCircle(sketch, "E126", {"center": v(0, 0) * mm, "radius": 5 * mm});
            skSolve(sketch);
        }
        {
            var Q1;
            {var subQ0=sQuery(id+"F56.wireOp",EDGE,"E126");var subQ44=makeQuery(id+"F56.imprint","INTERSECT",VERTEX,{"derivedFrom":[makeQuery(id+"F53.opExtrude","CAP_EDGE",EDGE,{"disambiguationData":[OSD([sQuery(id+"F52.wireOp",EDGE,"E121.2.5.0")])],"isStart":false}),subQ0]});Q1=makeQuery(id+"F56.imprint","IMPRINT",FACE,{"disambiguationData":[TD([[makeQuery(id+"F56.imprint","IMPRINT",EDGE,{"disambiguationData":[TD([[subQ44,-1.0]])],"derivedFrom":subQ0}),1.0]])]});}
            var Q2;
            Q2=makeQuery(id+"F55.imprint","IMPRINT",FACE,{"disambiguationData":[TD([[makeQuery(id+"F55.imprint","IMPRINT",EDGE,{"derivedFrom":sQuery(id+"F55.wireOp",EDGE,"E125")}),1.0]])]});
            loft(context, id + "F57", {"operationType" : NewBodyOperationType.ADD, "sheetProfilesArray" : [{ "sheetProfileEntities" : qUnion([Q1]) }, { "sheetProfileEntities" : qUnion([Q2]) }]});
        }
        {
            var Q0;
            Q0=makeQuery(id+"F57.opLoft","CAP_FACE",FACE,{"disambiguationData":[OSD([makeQuery(id+"F55.imprint","IMPRINT",FACE,{"disambiguationData":[TD([[makeQuery(id+"F55.imprint","IMPRINT",EDGE,{"derivedFrom":sQuery(id+"F55.wireOp",EDGE,"E125")}),1.0]])]})])],"isStart":true});
            var sketch = newSketch(context, id + "F58", { "sketchPlane" : qUnion([Q0])});
            skCircle(sketch, "E127", {"center": v(0, 0) * mm, "radius": 2 * mm});
            skSolve(sketch);
        }
        {
            var Q0;
            Q0=qSketchRegion(id+"F58",true);
            extrude(context, id + "F59", {"entities" : qUnion([Q0]), "operationType" : NewBodyOperationType.ADD, "depth" : 5 * mm});
        }
        {
            var Q0;
            {var subQ0=sQuery(id+"F0.wireOp",EDGE,"E0.right");var subQ1=sQuery(id+"F0.wireOp",EDGE,"E0.bottom");Q0=makeQuery(id+"F3.boolean.opBoolean","SPLIT",FACE,{"disambiguationData":[TD([makeQuery(id+"F1.opExtrude","SWEPT_FACE",FACE,{"disambiguationData":[OSD([subQ0])]})])],"derivedFrom":makeQuery(id+"F1.opExtrude","CAP_FACE",FACE,{"disambiguationData":[OSD([subQ1,sQuery(id+"F0.wireOp",EDGE,"E0.top"),sQuery(id+"F0.wireOp",EDGE,"E0.left"),subQ0])],"isStart":false})});}
            var sketch = newSketch(context, id + "F60", { "sketchPlane" : qUnion([Q0])});
            skLineSegment(sketch, "E128", {"start": v(-16.43, 20.44) * mm, "end": v(-16.42, -4.94) * mm});
            skLineSegment(sketch, "E129", {"start": v(-17.93, 22.85) * mm, "end": v(-17.92, -7.35) * mm});
            skLineSegment(sketch, "E130", {"start": v(-19.93, 24.38) * mm, "end": v(-19.93, -8.88) * mm});
            skLineSegment(sketch, "E131", {"start": v(-23.3, 25.25) * mm, "end": v(-23.3, -9.75) * mm});
            skArc(sketch, "E132", {"start": v(-16.43, 20.44) * mm, "mid": v(-19.12, 23.91) * mm, "end": v(-23.3, 25.25) * mm});
            skPoint(sketch, "E132.third.point", {"position": v(-29.25, 13.33) * mm});
            skPoint(sketch, "E133", {"position": v(-15.93, 17.75) * mm});
            skArc(sketch, "E134", {"start": v(-15.93, 17.75) * mm, "mid": v(-16.05, 19.12) * mm, "end": v(-16.43, 20.44) * mm});
            skPoint(sketch, "E135.end.orphan", {"position": v(-21.42, -9.75) * mm});
            skLineSegment(sketch, "E136", {"start": v(-21.42, -9.48) * mm, "end": v(-21.42, 24.98) * mm});
            skPoint(sketch, "E137.first.point", {"position": v(-15.92, -2.25) * mm});
            skPoint(sketch, "E137.third.point", {"position": v(-28.91, 2.76) * mm});
            skArc(sketch, "E138.trimOffspring", {"start": v(-23.3, -9.75) * mm, "mid": v(-18.07, -7.52) * mm, "end": v(-15.92, -2.25) * mm});
            skLineSegment(sketch, "E139", {"start": v(-15.93, 17.75) * mm, "end": v(-15.92, -2.25) * mm});
            skSolve(sketch);
        }
        {
            var Q0;
            Q0=makeQuery(id+"F23.opExtrude","CAP_EDGE",EDGE,{"disambiguationData":[OSD([sQuery(id+"F22.wireOp",EDGE,"E68.left")])],"isStart":false});
            fillet(context, id + "F61", {"entities" : qUnion([Q0]), "radius" : 5 * mm, "tangentPropagation" : true, "allowEdgeOverflow" : false});
        }
        {
            var Q0;
            Q0=makeQuery(id+"F23.opExtrude","CAP_EDGE",EDGE,{"disambiguationData":[OSD([sQuery(id+"F22.wireOp",EDGE,"E68.left")])],"isStart":true});
            var Q1;
            Q1=makeQuery(id+"F23.opExtrude","CAP_EDGE",EDGE,{"disambiguationData":[OSD([sQuery(id+"F22.wireOp",EDGE,"E68.right")])],"isStart":true});
            var Q2;
            Q2=makeQuery(id+"F23.opExtrude","CAP_EDGE",EDGE,{"disambiguationData":[OSD([sQuery(id+"F22.wireOp",EDGE,"E68.right")])],"isStart":false});
            var Q3;
            Q3=makeQuery(id+"F19.opExtrude","CAP_EDGE",EDGE,{"disambiguationData":[OSD([sQuery(id+"F18.wireOp",EDGE,"E63")])],"isStart":false});
            var Q4;
            Q4=makeQuery(id+"F19.opExtrude","CAP_EDGE",EDGE,{"disambiguationData":[OSD([sQuery(id+"F18.wireOp",EDGE,"E61")])],"isStart":false});
            var Q5;
            Q5=makeQuery(id+"F17.opExtrude","CAP_EDGE",EDGE,{"disambiguationData":[OSD([sQuery(id+"F16.wireOp",EDGE,"E59")])],"isStart":false});
            var Q6;
            Q6=makeQuery(id+"F15.opExtrude","CAP_EDGE",EDGE,{"disambiguationData":[OSD([sQuery(id+"F14.wireOp",EDGE,"E54")])],"isStart":false});
            fillet(context, id + "F62", {"entities" : qUnion([Q0, Q1, Q2, Q3, Q4, Q5, Q6]), "radius" : 5 * mm, "tangentPropagation" : true, "allowEdgeOverflow" : false});
        }
        {
            var Q0;
            {var subQ5=sQuery(id+"F60.wireOp",EDGE,"E136");Q0=makeQuery(id+"F60.imprint","IMPRINT",FACE,{"disambiguationData":[TD([[makeQuery(id+"F60.imprint","IMPRINT",EDGE,{"derivedFrom":subQ5}),1.0]])]});}
            extrude(context, id + "F63", {"entities" : qUnion([Q0]), "operationType" : NewBodyOperationType.REMOVE, "oppositeDirection" : true, "depth" : 2 * mm});
        }
        {
            var Q0;
            {var subQ0=sQuery(id+"F60.wireOp",EDGE,"E129");Q0=makeQuery(id+"F60.imprint","IMPRINT",FACE,{"disambiguationData":[TD([[makeQuery(id+"F60.imprint","IMPRINT",EDGE,{"derivedFrom":subQ0}),-1.0]])]});}
            var Q1;
            {var subQ0=sQuery(id+"F60.wireOp",EDGE,"E128");Q1=makeQuery(id+"F60.imprint","IMPRINT",FACE,{"disambiguationData":[TD([[makeQuery(id+"F60.imprint","IMPRINT",EDGE,{"derivedFrom":subQ0}),1.0]])]});}
            extrude(context, id + "F64", {"entities" : qUnion([Q0, Q1]), "operationType" : NewBodyOperationType.REMOVE, "oppositeDirection" : true, "depth" : 2 * mm});
        }
        {
            var Q0;
            Q0=makeQuery(id+"F1.opExtrude","CAP_EDGE",EDGE,{"disambiguationData":[OSD([sQuery(id+"F0.wireOp",EDGE,"E0.right")])],"isStart":false});
            fillet(context, id + "F65", {"entities" : qUnion([Q0]), "radius" : 5 * mm, "tangentPropagation" : true, "allowEdgeOverflow" : false});
        }
        {
            var Q0;
            {var subQ0=sQuery(id+"F0.wireOp",EDGE,"E0.left");var subQ1=sQuery(id+"F0.wireOp",EDGE,"E0.bottom");Q0=makeQuery(id+"F3.boolean.opBoolean","SPLIT",FACE,{"disambiguationData":[TD([makeQuery(id+"F1.opExtrude","SWEPT_FACE",FACE,{"disambiguationData":[OSD([subQ0])]})])],"derivedFrom":makeQuery(id+"F1.opExtrude","CAP_FACE",FACE,{"disambiguationData":[OSD([subQ1,sQuery(id+"F0.wireOp",EDGE,"E0.top"),subQ0,sQuery(id+"F0.wireOp",EDGE,"E0.right")])],"isStart":false})});}
            var sketch = newSketch(context, id + "F66", { "sketchPlane" : qUnion([Q0])});
            skLineSegment(sketch, "E140", {"start": v(16.42, 20.44) * mm, "end": v(16.42, -4.94) * mm});
            skLineSegment(sketch, "E141", {"start": v(17.92, 22.85) * mm, "end": v(17.93, -7.35) * mm});
            skLineSegment(sketch, "E142", {"start": v(17.93, -7.35) * mm, "end": v(17.9, -7) * mm});
            skLineSegment(sketch, "E143", {"start": v(19.92, 24.38) * mm, "end": v(19.93, -8.88) * mm});
            skLineSegment(sketch, "E144", {"start": v(21.42, 24.98) * mm, "end": v(21.43, -9.48) * mm});
            skPoint(sketch, "E145.endSnap0", {"position": v(27.98, -9.75) * mm});
            skPoint(sketch, "E146.first.point", {"position": v(15.92, 17.75) * mm});
            skPoint(sketch, "E146.third.point", {"position": v(30.03, 14.4) * mm});
            skPoint(sketch, "E147.first.point", {"position": v(15.92, -2.25) * mm});
            skPoint(sketch, "E147.third.point", {"position": v(29.77, 3.26) * mm});
            skLineSegment(sketch, "E148", {"start": v(15.92, 17.75) * mm, "end": v(15.92, -2.25) * mm});
            skArc(sketch, "E149", {"start": v(21.42, 24.98) * mm, "mid": v(17.46, 22.3) * mm, "end": v(15.92, 17.75) * mm});
            skArc(sketch, "E150", {"start": v(15.92, -2.25) * mm, "mid": v(17.46, -6.8) * mm, "end": v(21.43, -9.48) * mm});
            skPoint(sketch, "E151.orphan", {"position": v(23.43, -9.75) * mm});
            skLineSegment(sketch, "E152", {"start": v(23.42, 25.25) * mm, "end": v(23.43, -9.75) * mm});
            skArc(sketch, "E153", {"start": v(23.42, 25.25) * mm, "mid": v(18.12, 23.05) * mm, "end": v(15.92, 17.75) * mm});
            skArc(sketch, "E154", {"start": v(15.92, -2.25) * mm, "mid": v(18.12, -7.55) * mm, "end": v(23.43, -9.75) * mm});
            skLineSegment(sketch, "E155", {"start": v(21.42, 24.98) * mm, "end": v(23.42, 24.98) * mm});
            skLineSegment(sketch, "E156", {"start": v(21.43, -9.48) * mm, "end": v(23.43, -9.48) * mm});
            skSolve(sketch);
        }
        {
            var Q0;
            {var subQ6=sQuery(id+"F66.wireOp",EDGE,"E143");Q0=makeQuery(id+"F66.imprint","IMPRINT",FACE,{"disambiguationData":[TD([[makeQuery(id+"F66.imprint","IMPRINT",EDGE,{"derivedFrom":subQ6}),-1.0]])]});}
            var Q1;
            {var subQ3=sQuery(id+"F66.wireOp",EDGE,"E140");Q1=makeQuery(id+"F66.imprint","IMPRINT",FACE,{"disambiguationData":[TD([[makeQuery(id+"F66.imprint","IMPRINT",EDGE,{"derivedFrom":subQ3}),-1.0]])]});}
            extrude(context, id + "F67", {"entities" : qUnion([Q0, Q1]), "operationType" : NewBodyOperationType.REMOVE, "oppositeDirection" : true, "depth" : 2 * mm});
        }
        {
            var Q0;
            Q0=makeQuery(id+"F1.opExtrude","CAP_EDGE",EDGE,{"disambiguationData":[OSD([sQuery(id+"F0.wireOp",EDGE,"E0.left")])],"isStart":false});
            fillet(context, id + "F68", {"entities" : qUnion([Q0]), "radius" : 5 * mm, "tangentPropagation" : true, "allowEdgeOverflow" : false});
        }
        {
            var Q0;
            Q0=makeQuery(id+"F66.imprint","IMPRINT",FACE,{"disambiguationData":[TD([[makeQuery(id+"F66.imprint","IMPRINT",EDGE,{"derivedFrom":sQuery(id+"F66.wireOp",EDGE,"E144")}),1.0]])]});
            extrude(context, id + "F69", {"entities" : qUnion([Q0]), "operationType" : NewBodyOperationType.REMOVE, "oppositeDirection" : true, "depth" : 2 * mm});
        }
        {
            var Q0;
            {var subQ3=sQuery(id+"F66.wireOp",EDGE,"E156");Q0=makeQuery(id+"F66.imprint","IMPRINT",FACE,{"disambiguationData":[TD([[makeQuery(id+"F66.imprint","IMPRINT",EDGE,{"derivedFrom":subQ3}),-1.0]])]});}
            extrude(context, id + "F70", {"entities" : qUnion([Q0]), "operationType" : NewBodyOperationType.REMOVE, "oppositeDirection" : true, "depth" : 2 * mm});
        }
        {
            var Q0;
            Q0=makeQuery(id+"F6.boolean.opBoolean","MERGE",EDGE,{"derivedFrom":[makeQuery(id+"F1.opExtrude","CAP_EDGE",EDGE,{"disambiguationData":[OSD([sQuery(id+"F0.wireOp",EDGE,"E0.right")])],"isStart":true}),makeQuery(id+"F6.opExtrude","SWEPT_EDGE",EDGE,{"disambiguationData":[OSD([sQuery(id+"F5.wireOp",EDGE,"E31.top"),sQuery(id+"F5.wireOp",EDGE,"E31.left")])]})]});
            fillet(context, id + "F71", {"entities" : qUnion([Q0]), "radius" : 5 * mm, "tangentPropagation" : true, "allowEdgeOverflow" : false});
        }
        {
            var Q0;
            Q0=makeQuery(id+"F6.boolean.opBoolean","MERGE",EDGE,{"derivedFrom":[makeQuery(id+"F1.opExtrude","CAP_EDGE",EDGE,{"disambiguationData":[OSD([sQuery(id+"F0.wireOp",EDGE,"E0.left")])],"isStart":true}),makeQuery(id+"F6.opExtrude","SWEPT_EDGE",EDGE,{"disambiguationData":[OSD([sQuery(id+"F5.wireOp",EDGE,"E31.top"),sQuery(id+"F5.wireOp",EDGE,"E31.right")])]})]});
            fillet(context, id + "F72", {"entities" : qUnion([Q0]), "radius" : 5 * mm, "tangentPropagation" : true, "allowEdgeOverflow" : false});
        }
        {
            var Q0;
            Q0=makeQuery(id+"F6.boolean.opBoolean","MERGE",FACE,{"derivedFrom":[makeQuery(id+"F3.boolean.opBoolean","MERGE",FACE,{"derivedFrom":[makeQuery(id+"F1.opExtrude","SWEPT_FACE",FACE,{"disambiguationData":[OSD([sQuery(id+"F0.wireOp",EDGE,"E0.right")])]}),makeQuery(id+"F3.opExtrude","SWEPT_FACE",FACE,{"disambiguationData":[OSD([sQuery(id+"F2.wireOp",EDGE,"E5")])]})]}),makeQuery(id+"F6.opExtrude","SWEPT_FACE",FACE,{"disambiguationData":[OSD([sQuery(id+"F5.wireOp",EDGE,"E31.left")])]})]});
            var sketch = newSketch(context, id + "F73", { "sketchPlane" : qUnion([Q0])});
            skLineSegment(sketch, "E157", {"start": v(7, 25.25) * mm, "end": v(7, -9.75) * mm});
            skLineSegment(sketch, "E158", {"start": v(5, 25.25) * mm, "end": v(5, -9.75) * mm});
            skLineSegment(sketch, "E159", {"start": v(3.5, 25.25) * mm, "end": v(3.5, -9.75) * mm});
            skLineSegment(sketch, "E160", {"start": v(8.5, 25.25) * mm, "end": v(8.5, -9.75) * mm});
            skLineSegment(sketch, "E161", {"start": v(1.5, 25.25) * mm, "end": v(1.5, -9.75) * mm});
            skLineSegment(sketch, "E162", {"start": v(0, 25.25) * mm, "end": v(0, -9.75) * mm});
            skLineSegment(sketch, "E163", {"start": v(-2, 25.25) * mm, "end": v(-2, -9.75) * mm});
            skLineSegment(sketch, "E164", {"start": v(-3.5, 25.25) * mm, "end": v(-3.5, -9.75) * mm});
            skLineSegment(sketch, "E165", {"start": v(-5.5, 25.25) * mm, "end": v(-5.5, -9.75) * mm});
            skLineSegment(sketch, "E166", {"start": v(-7, 25.25) * mm, "end": v(-7, -9.75) * mm});
            skLineSegment(sketch, "E167", {"start": v(-9, 25.25) * mm, "end": v(-9, -9.75) * mm});
            skLineSegment(sketch, "E168", {"start": v(-10.5, 25.25) * mm, "end": v(-10.5, -9.75) * mm});
            skLineSegment(sketch, "E169", {"start": v(-10.5, 25.25) * mm, "end": v(8.5, 25.25) * mm});
            skLineSegment(sketch, "E170", {"start": v(-10.5, -9.75) * mm, "end": v(10.5, -9.75) * mm});
            skLineSegment(sketch, "E171", {"start": v(10.5, -9.75) * mm, "end": v(10.5, 25.25) * mm});
            skLineSegment(sketch, "E172", {"start": v(10.5, 25.25) * mm, "end": v(8.5, 25.25) * mm});
            skSolve(sketch);
        }
        {
            var Q0;
            {var subQ0=sQuery(id+"F73.wireOp",EDGE,"E166");Q0=makeQuery(id+"F73.imprint","IMPRINT",FACE,{"disambiguationData":[TD([[makeQuery(id+"F73.imprint","IMPRINT",EDGE,{"derivedFrom":subQ0}),-1.0]])]});}
            var Q1;
            {var subQ0=sQuery(id+"F73.wireOp",EDGE,"E164");Q1=makeQuery(id+"F73.imprint","IMPRINT",FACE,{"disambiguationData":[TD([[makeQuery(id+"F73.imprint","IMPRINT",EDGE,{"derivedFrom":subQ0}),-1.0]])]});}
            var Q2;
            {var subQ0=sQuery(id+"F73.wireOp",EDGE,"E162");Q2=makeQuery(id+"F73.imprint","IMPRINT",FACE,{"disambiguationData":[TD([[makeQuery(id+"F73.imprint","IMPRINT",EDGE,{"derivedFrom":subQ0}),-1.0]])]});}
            var Q3;
            {var subQ0=sQuery(id+"F73.wireOp",EDGE,"E159");Q3=makeQuery(id+"F73.imprint","IMPRINT",FACE,{"disambiguationData":[TD([[makeQuery(id+"F73.imprint","IMPRINT",EDGE,{"derivedFrom":subQ0}),-1.0]])]});}
            var Q4;
            {var subQ0=sQuery(id+"F73.wireOp",EDGE,"E157");Q4=makeQuery(id+"F73.imprint","IMPRINT",FACE,{"disambiguationData":[TD([[makeQuery(id+"F73.imprint","IMPRINT",EDGE,{"derivedFrom":subQ0}),-1.0]])]});}
            var Q5;
            {var subQ0=sQuery(id+"F73.wireOp",EDGE,"E160");Q5=makeQuery(id+"F73.imprint","IMPRINT",FACE,{"disambiguationData":[TD([[makeQuery(id+"F73.imprint","IMPRINT",EDGE,{"derivedFrom":subQ0}),1.0]])]});}
            extrude(context, id + "F74", {"entities" : qUnion([Q0, Q1, Q2, Q3, Q4, Q5]), "operationType" : NewBodyOperationType.REMOVE, "oppositeDirection" : true, "depth" : 2 * mm});
        }
        {
            var Q0;
            Q0=makeQuery(id+"F6.boolean.opBoolean","MERGE",FACE,{"derivedFrom":[makeQuery(id+"F3.boolean.opBoolean","MERGE",FACE,{"derivedFrom":[makeQuery(id+"F1.opExtrude","SWEPT_FACE",FACE,{"disambiguationData":[OSD([sQuery(id+"F0.wireOp",EDGE,"E0.left")])]}),makeQuery(id+"F3.opExtrude","SWEPT_FACE",FACE,{"disambiguationData":[OSD([sQuery(id+"F2.wireOp",EDGE,"E6")])]})]}),makeQuery(id+"F6.opExtrude","SWEPT_FACE",FACE,{"disambiguationData":[OSD([sQuery(id+"F5.wireOp",EDGE,"E31.right")])]})]});
            var sketch = newSketch(context, id + "F75", { "sketchPlane" : qUnion([Q0])});
            skLineSegment(sketch, "E173", {"start": v(-10.5, 25.25) * mm, "end": v(-10.5, -9.75) * mm});
            skLineSegment(sketch, "E174", {"start": v(-10.5, -9.75) * mm, "end": v(10.5, -9.75) * mm});
            skLineSegment(sketch, "E175", {"start": v(10.5, -9.75) * mm, "end": v(10.5, 25.25) * mm});
            skLineSegment(sketch, "E176", {"start": v(10.5, 25.25) * mm, "end": v(-10.5, 25.25) * mm});
            skLineSegment(sketch, "E177", {"start": v(-8.5, 25.25) * mm, "end": v(-8.5, -9.75) * mm});
            skLineSegment(sketch, "E178", {"start": v(-7, 25.25) * mm, "end": v(-7, -9.75) * mm});
            skLineSegment(sketch, "E179", {"start": v(-5, 25.25) * mm, "end": v(-5, -9.75) * mm});
            skLineSegment(sketch, "E180", {"start": v(-3.5, 25.25) * mm, "end": v(-3.5, -9.75) * mm});
            skLineSegment(sketch, "E181", {"start": v(-1.5, 25.25) * mm, "end": v(-1.5, -9.75) * mm});
            skLineSegment(sketch, "E182", {"start": v(0, 25.25) * mm, "end": v(0, -9.75) * mm});
            skLineSegment(sketch, "E183", {"start": v(2, 25.25) * mm, "end": v(2, -9.75) * mm});
            skLineSegment(sketch, "E184", {"start": v(3.5, 25.25) * mm, "end": v(3.5, -9.75) * mm});
            skLineSegment(sketch, "E185", {"start": v(5.5, 25.25) * mm, "end": v(5.5, -9.75) * mm});
            skLineSegment(sketch, "E186", {"start": v(9, 25.25) * mm, "end": v(9, -9.75) * mm});
            skLineSegment(sketch, "E187", {"start": v(7, 25.25) * mm, "end": v(7, -9.75) * mm});
            skSolve(sketch);
        }
        {
            var Q0;
            {var subQ0=sQuery(id+"F75.wireOp",EDGE,"E173");Q0=makeQuery(id+"F75.imprint","IMPRINT",FACE,{"disambiguationData":[TD([[makeQuery(id+"F75.imprint","IMPRINT",EDGE,{"derivedFrom":subQ0}),1.0]])]});}
            var Q1;
            {var subQ0=sQuery(id+"F75.wireOp",EDGE,"E178");Q1=makeQuery(id+"F75.imprint","IMPRINT",FACE,{"disambiguationData":[TD([[makeQuery(id+"F75.imprint","IMPRINT",EDGE,{"derivedFrom":subQ0}),1.0]])]});}
            var Q2;
            {var subQ0=sQuery(id+"F75.wireOp",EDGE,"E180");Q2=makeQuery(id+"F75.imprint","IMPRINT",FACE,{"disambiguationData":[TD([[makeQuery(id+"F75.imprint","IMPRINT",EDGE,{"derivedFrom":subQ0}),1.0]])]});}
            var Q3;
            {var subQ0=sQuery(id+"F75.wireOp",EDGE,"E182");Q3=makeQuery(id+"F75.imprint","IMPRINT",FACE,{"disambiguationData":[TD([[makeQuery(id+"F75.imprint","IMPRINT",EDGE,{"derivedFrom":subQ0}),1.0]])]});}
            var Q4;
            {var subQ0=sQuery(id+"F75.wireOp",EDGE,"E184");Q4=makeQuery(id+"F75.imprint","IMPRINT",FACE,{"disambiguationData":[TD([[makeQuery(id+"F75.imprint","IMPRINT",EDGE,{"derivedFrom":subQ0}),1.0]])]});}
            var Q5;
            {var subQ0=sQuery(id+"F75.wireOp",EDGE,"E186");Q5=makeQuery(id+"F75.imprint","IMPRINT",FACE,{"disambiguationData":[TD([[makeQuery(id+"F75.imprint","IMPRINT",EDGE,{"derivedFrom":subQ0}),-1.0]])]});}
            extrude(context, id + "F76", {"entities" : qUnion([Q0, Q1, Q2, Q3, Q4, Q5]), "operationType" : NewBodyOperationType.REMOVE, "oppositeDirection" : true, "depth" : 2 * mm});
        }
    });
